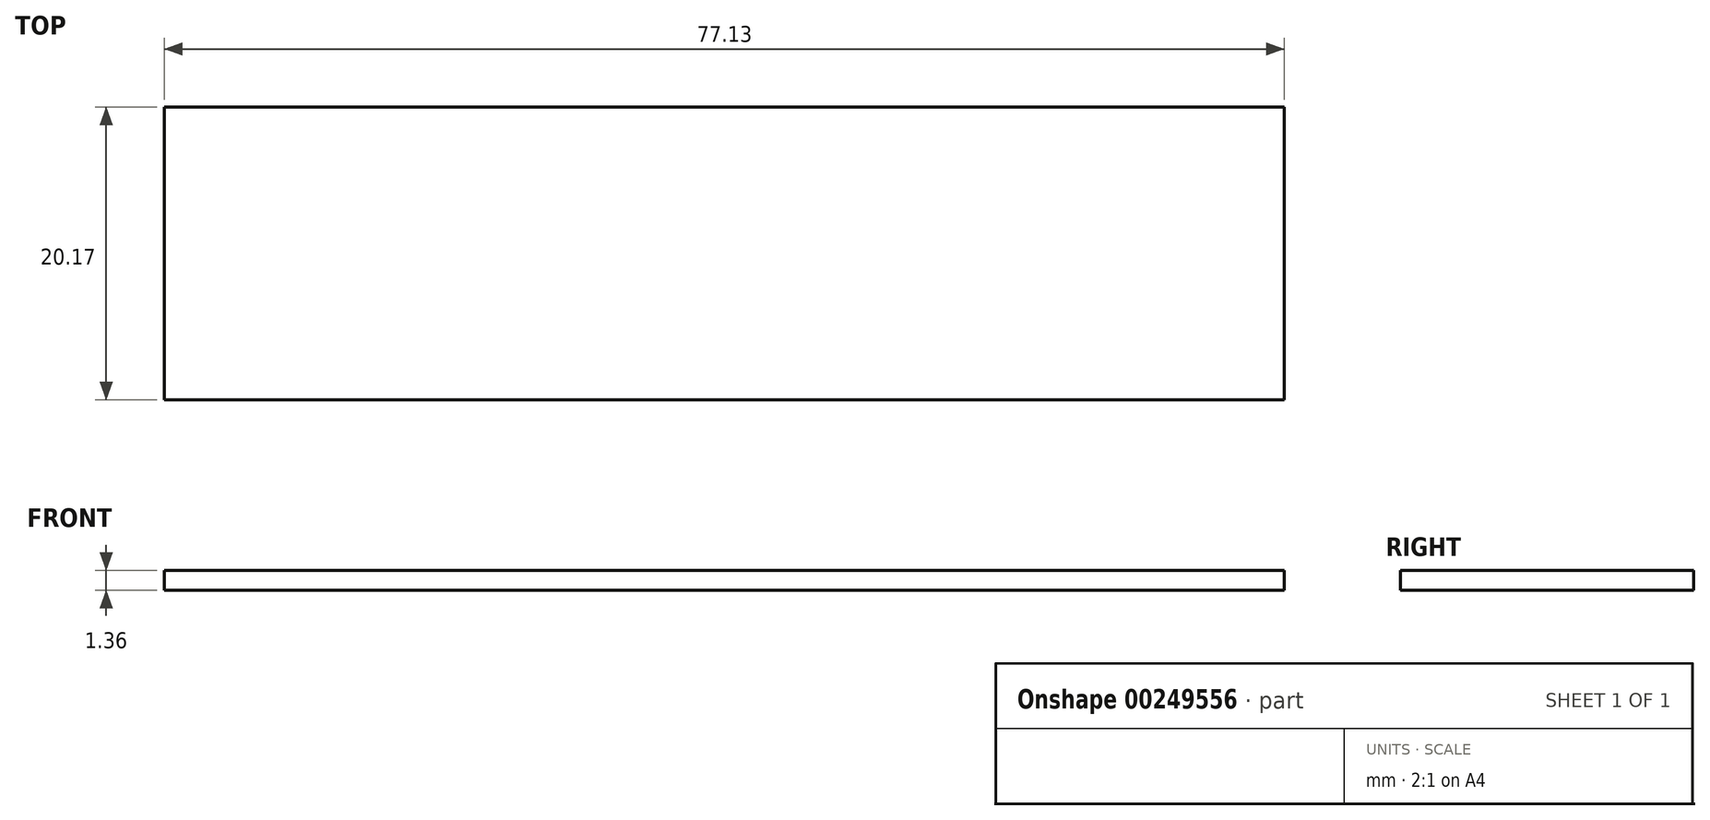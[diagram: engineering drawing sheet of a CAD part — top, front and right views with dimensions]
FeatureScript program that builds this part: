
annotation { "Feature Type Name" : "Feature", "Feature Type Description" : "" }
export const myFeature = defineFeature(function(context is Context, id is Id, definition is map)
    precondition{}
    {
        {
            var Q0;
            Q0=qCreatedBy(makeId("Top.planeOp"),FACE);
            var sketch = newSketch(context, id + "F0", { "sketchPlane" : qUnion([Q0])});
            skLineSegment(sketch, "E0", {"start": v(0, 0) * mm, "end": v(0, 20.17) * mm});
            skLineSegment(sketch, "E1", {"start": v(0, 20.17) * mm, "end": v(77.13, 20.17) * mm});
            skLineSegment(sketch, "E2", {"start": v(0, 0) * mm, "end": v(77.13, 0) * mm});
            skLineSegment(sketch, "E3", {"start": v(77.13, 20.17) * mm, "end": v(77.13, 0) * mm});
            skSolve(sketch);
        }
        {
            var Q0;
            Q0 = qSketchRegion(id + "F0", true);
            extrude(context, id + "F1", {"entities" : qUnion([Q0]), "depth" : 1.36 * mm});
        }
    });
